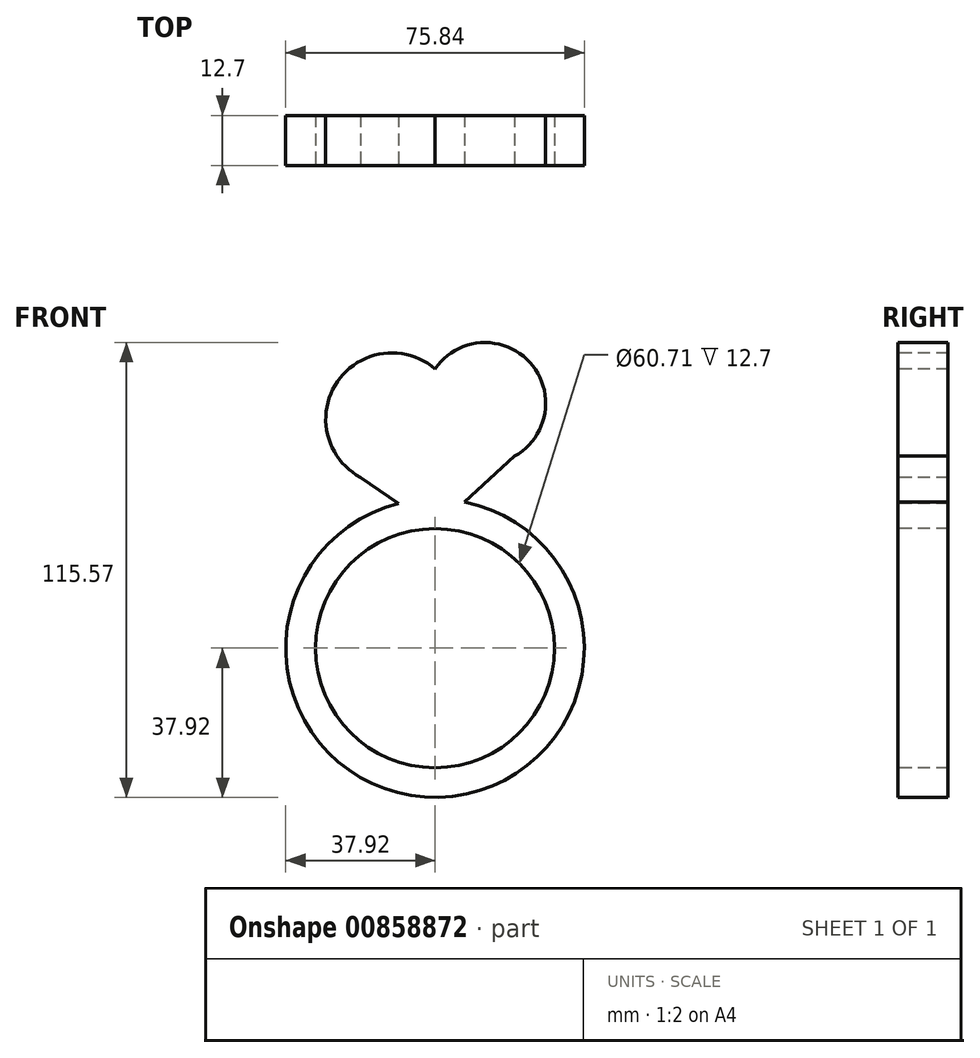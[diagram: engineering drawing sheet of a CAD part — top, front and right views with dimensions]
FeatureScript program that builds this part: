
annotation { "Feature Type Name" : "Feature", "Feature Type Description" : "" }
export const myFeature = defineFeature(function(context is Context, id is Id, definition is map)
    precondition{}
    {
        {
            var Q0;
            Q0=qCreatedBy(makeId("Front.planeOp"),FACE);
            var sketch = newSketch(context, id + "F0", { "sketchPlane" : qUnion([Q0])});
            skCircle(sketch, "E0", {"center": v(0, 0) * mm, "radius": 37.92 * mm});
            skCircle(sketch, "E1", {"center": v(0, 0) * mm, "radius": 30.36 * mm});
            skLineSegment(sketch, "E2", {"start": v(0, 30.36) * mm, "end": v(25.4, 53.49) * mm});
            skLineSegment(sketch, "E3", {"start": v(25.4, 53.49) * mm, "end": v(0, 70.97) * mm});
            skLineSegment(sketch, "E4", {"start": v(0, 30.36) * mm, "end": v(-21.87, 45.41) * mm});
            skLineSegment(sketch, "E5", {"start": v(-21.87, 45.41) * mm, "end": v(0, 70.97) * mm});
            skCircle(sketch, "E6", {"center": v(-10.94, 58.2) * mm, "radius": 16.82 * mm});
            skCircle(sketch, "E7", {"center": v(12.7, 62.23) * mm, "radius": 15.42 * mm});
            skSolve(sketch);
        }
        {
            var Q0;
            Q0=qSketchRegion(id+"F0",true);
            extrude(context, id + "F1", {"entities" : qUnion([Q0]), "oppositeDirection" : true, "depth" : 12.7 * mm, "offsetDistance" : 25.4 * mm});
        }
        {
            var Q0;
            Q0=qSketchRegion(id+"F0",true);
            var Q1;
            Q1=makeQuery(id+"F1.opExtrude","CAP_FACE",FACE,{"disambiguationData":[OSD([sQuery(id+"F0.wireOp",EDGE,"E0"),sQuery(id+"F0.wireOp",EDGE,"E1"),sQuery(id+"F0.wireOp",EDGE,"E2"),sQuery(id+"F0.wireOp",EDGE,"E4"),sQuery(id+"F0.wireOp",EDGE,"E6"),sQuery(id+"F0.wireOp",EDGE,"E7")])],"isStart":true});
            extrude(context, id + "F2", {"entities" : qUnion([Q0, Q1]), "operationType" : NewBodyOperationType.ADD, "oppositeDirection" : true, "depth" : 12.7 * mm, "offsetDistance" : 25.4 * mm});
        }
    });
